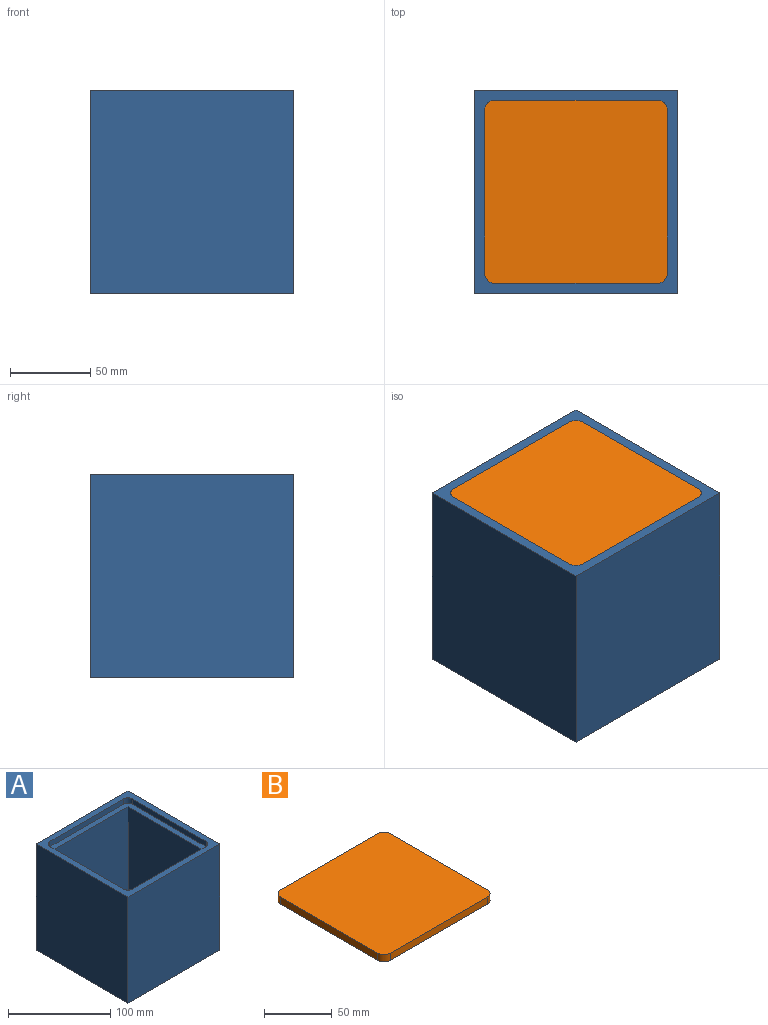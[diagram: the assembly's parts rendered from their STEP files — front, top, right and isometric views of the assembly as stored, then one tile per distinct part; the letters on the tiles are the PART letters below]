
ASSEMBLY  parts=2 mates=1
PART A: 19 faces, bbox 127x127x127 mm
  f0: plane 127x127mm, normal (1,0,0), area 16129mm2, adj f1,f3,f4,f5
  f1: plane 127x127mm, normal (0,1,0), area 16129mm2, adj f0,f2,f4,f5
  f2: plane 127x127mm, normal (-1,0,0), area 16129mm2, adj f1,f3,f4,f5
  f3: plane 127x127mm, normal (0,-1,0), area 16129mm2, adj f0,f2,f4,f5
  f4: plane 127x127mm, normal (0,0,1), area 3099.1mm2, adj f0,f1,f2,f3,f6,f7,f8,f9
  f5: plane 127x127mm, normal (0,0,-1), area 5806.4mm2, adj f0,f1,f2,f3,f15,f16,f17,f18
  f6: cylinder r=6.35mm len=6.35mm, axis (0,0,1), area 63.3mm2, adj f4,f7,f13,f14
  f7: plane 101.6x6.35mm, normal (0,-1,0), area 645.2mm2, adj f4,f6,f8,f14
  f8: cylinder r=6.35mm len=6.35mm, axis (0,0,1), area 63.3mm2, adj f4,f7,f9,f14
  f9: plane 101.6x6.35mm, normal (1,0,0), area 645.2mm2, adj f4,f8,f10,f14
  f10: cylinder r=6.35mm len=6.35mm, axis (0,0,1), area 63.3mm2, adj f4,f9,f11,f14
  f11: plane 101.6x6.35mm, normal (0,1,0), area 645.2mm2, adj f4,f10,f12,f14
  f12: cylinder r=6.35mm len=6.35mm, axis (0,0,1), area 63.3mm2, adj f4,f11,f13,f14
  f13: plane 101.6x6.35mm, normal (-1,0,0), area 645.2mm2, adj f4,f6,f12,f14
  f14: plane 114.3x114.3mm, normal (0,0,1), area 2707.3mm2, adj f6,f7,f8,f9,f10,f11,f12,f13
  f15: plane 120.65x101.6mm, normal (-1,0,0), area 12258mm2, adj f5,f14,f16,f18
  f16: plane 120.65x101.6mm, normal (0,-1,0), area 12258mm2, adj f5,f14,f15,f17
  f17: plane 120.65x101.6mm, normal (1,0,0), area 12258mm2, adj f5,f14,f16,f18
  f18: plane 120.65x101.6mm, normal (0,1,0), area 12258mm2, adj f5,f14,f15,f17
PART B: 10 faces, bbox 114.3x114.3x6.4 mm
  f0: cylinder r=6.35mm len=6.35mm, axis (0,0,-1), area 63.3mm2, adj f1,f7,f8,f9
  f1: plane 101.6x6.35mm, normal (0,1,0), area 645.2mm2, adj f0,f2,f8,f9
  f2: cylinder r=6.35mm len=6.35mm, axis (0,0,-1), area 63.3mm2, adj f1,f3,f8,f9
  f3: plane 101.6x6.35mm, normal (-1,0,0), area 645.2mm2, adj f2,f4,f8,f9
  f4: cylinder r=6.35mm len=6.35mm, axis (0,0,-1), area 63.3mm2, adj f3,f5,f8,f9
  f5: plane 101.6x6.35mm, normal (0,-1,0), area 645.2mm2, adj f4,f6,f8,f9
  f6: cylinder r=6.35mm len=6.35mm, axis (0,0,-1), area 63.3mm2, adj f5,f7,f8,f9
  f7: plane 101.6x6.35mm, normal (1,0,0), area 645.2mm2, adj f0,f6,f8,f9
  f8: plane 114.3x114.3mm, normal (0,0,1), area 13029.9mm2, adj f0,f1,f2,f3,f4,f5,f6,f7
  f9: plane 114.3x114.3mm, normal (0,0,-1), area 13029.9mm2, adj f0,f1,f2,f3,f4,f5,f6,f7
PLACE A t=(-76.65,-10.35,-12.64)mm
PLACE B t=(-76.65,-10.35,108.01)mm
MATE fastened B.f5 <-> A.f11  axis (0,-1,0) through (-76.65,-67.5,114.36)mm
